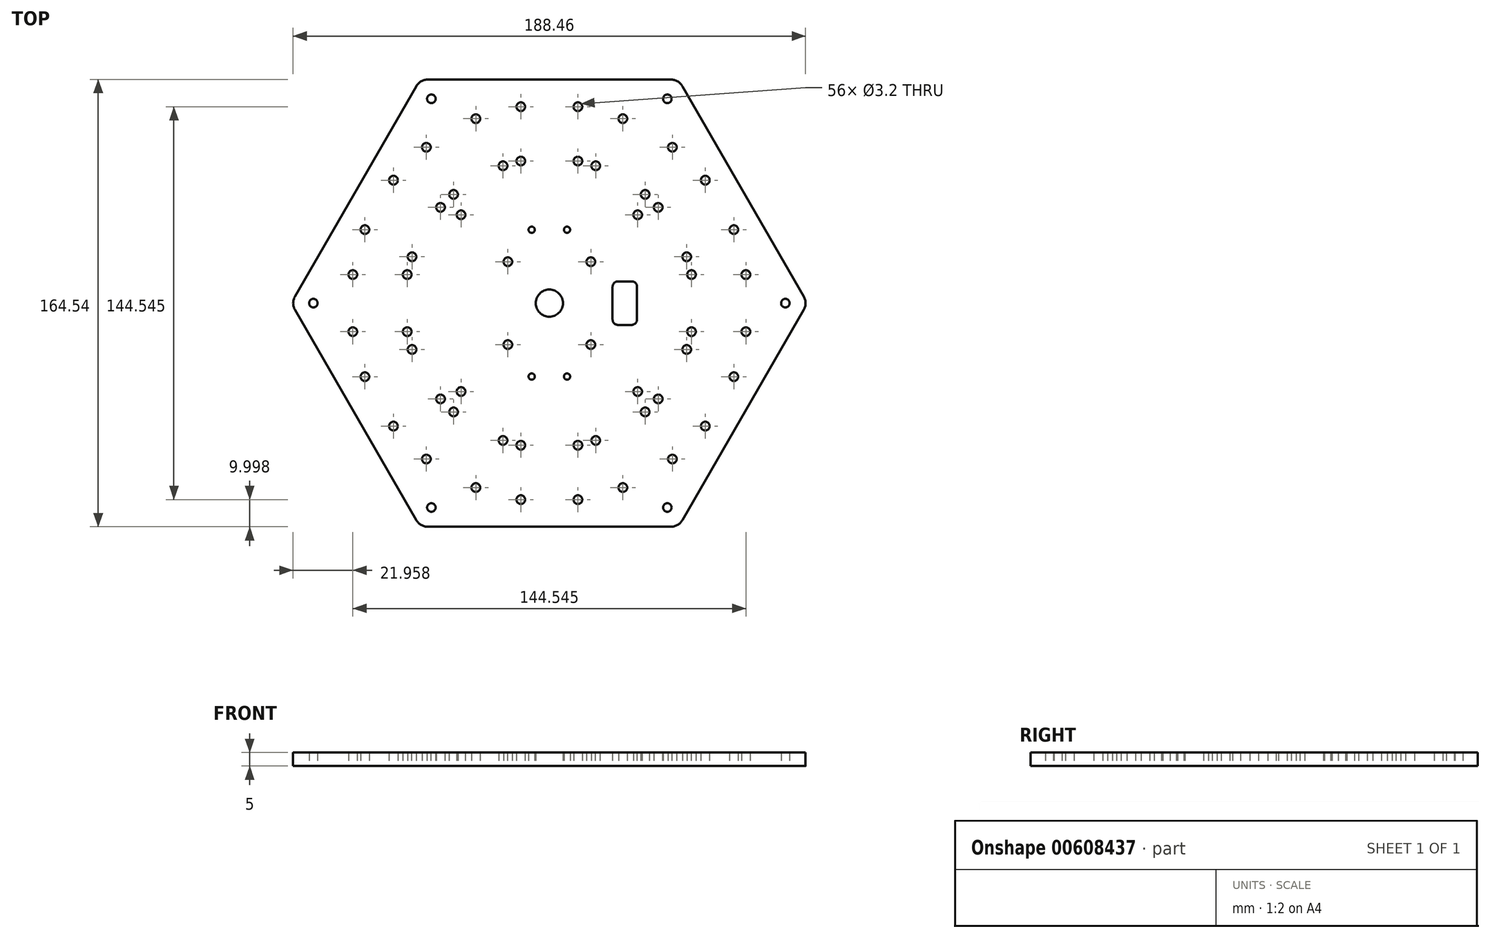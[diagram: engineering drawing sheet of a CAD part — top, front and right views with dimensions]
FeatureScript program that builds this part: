
annotation { "Feature Type Name" : "Feature", "Feature Type Description" : "" }
export const myFeature = defineFeature(function(context is Context, id is Id, definition is map)
    precondition{}
    {
        {
            var Q0;
            Q0=qCreatedBy(makeId("Top.planeOp"),FACE);
            var sketch = newSketch(context, id + "F0", { "sketchPlane" : qUnion([Q0])});
            skLineSegment(sketch, "E0.1", {"start": v(-48.94, -79.77) * mm, "end": v(-93.56, -2.5) * mm});
            skLineSegment(sketch, "E0.2", {"start": v(-93.56, 2.5) * mm, "end": v(-48.94, 79.77) * mm});
            skLineSegment(sketch, "E0.3", {"start": v(-44.61, 82.27) * mm, "end": v(44.61, 82.27) * mm});
            skLineSegment(sketch, "E0.4", {"start": v(48.94, 79.77) * mm, "end": v(93.56, 2.5) * mm});
            skLineSegment(sketch, "E0.5", {"start": v(93.56, -2.5) * mm, "end": v(48.94, -79.77) * mm});
            skPoint(sketch, "E0.cCircle.center.orphan", {"position": v(0, 0) * mm});
            skLineSegment(sketch, "E1", {"start": v(-44.61, -82.27) * mm, "end": v(44.61, -82.27) * mm});
            skPoint(sketch, "E2", {"position": v(-47.5, 82.27) * mm});
            skPoint(sketch, "E3", {"position": v(-43.4, 75.17) * mm});
            skCircle(sketch, "E4", {"center": v(-43.4, 75.17) * mm, "radius": 1.57 * mm});
            skCircle(sketch, "E5.1.0", {"center": v(-86.8, 0) * mm, "radius": 1.57 * mm});
            skCircle(sketch, "E5.2.0", {"center": v(-43.4, -75.17) * mm, "radius": 1.57 * mm});
            skCircle(sketch, "E5.3.0", {"center": v(43.4, -75.17) * mm, "radius": 1.57 * mm});
            skCircle(sketch, "E5.4.0", {"center": v(86.8, 0) * mm, "radius": 1.57 * mm});
            skCircle(sketch, "E5.5.0", {"center": v(43.4, 75.17) * mm, "radius": 1.57 * mm});
            skPoint(sketch, "E6", {"position": v(47.5, 82.27) * mm});
            skPoint(sketch, "E7", {"position": v(0, 82.27) * mm});
            skPoint(sketch, "E8", {"position": v(10.5, 82.27) * mm});
            skPoint(sketch, "E9", {"position": v(-10.5, 82.27) * mm});
            skPoint(sketch, "E10", {"position": v(-10.5, 72.27) * mm});
            skPoint(sketch, "E11", {"position": v(10.5, 72.27) * mm});
            skPoint(sketch, "E12", {"position": v(-10.5, 52.27) * mm});
            skPoint(sketch, "E13", {"position": v(10.5, 52.27) * mm});
            skCircle(sketch, "E14", {"center": v(-10.5, 72.27) * mm, "radius": 1.6 * mm});
            skCircle(sketch, "E15", {"center": v(10.5, 72.27) * mm, "radius": 1.6 * mm});
            skCircle(sketch, "E16", {"center": v(10.5, 52.27) * mm, "radius": 1.6 * mm});
            skCircle(sketch, "E17", {"center": v(-10.5, 52.27) * mm, "radius": 1.6 * mm});
            skPoint(sketch, "E18.1.0", {"position": v(-27.04, 67.84) * mm});
            skCircle(sketch, "E18.1.1", {"center": v(-27.04, 67.84) * mm, "radius": 1.6 * mm});
            skPoint(sketch, "E18.1.2", {"position": v(-45.23, 57.34) * mm});
            skCircle(sketch, "E18.1.3", {"center": v(-45.23, 57.34) * mm, "radius": 1.6 * mm});
            skPoint(sketch, "E18.1.4", {"position": v(-35.23, 40.02) * mm});
            skCircle(sketch, "E18.1.5", {"center": v(-35.23, 40.02) * mm, "radius": 1.6 * mm});
            skPoint(sketch, "E18.1.6", {"position": v(-17.04, 50.52) * mm});
            skCircle(sketch, "E18.1.7", {"center": v(-17.04, 50.52) * mm, "radius": 1.6 * mm});
            skPoint(sketch, "E18.2.0", {"position": v(-57.34, 45.23) * mm});
            skCircle(sketch, "E18.2.1", {"center": v(-57.34, 45.23) * mm, "radius": 1.6 * mm});
            skPoint(sketch, "E18.2.2", {"position": v(-67.84, 27.04) * mm});
            skCircle(sketch, "E18.2.3", {"center": v(-67.84, 27.04) * mm, "radius": 1.6 * mm});
            skPoint(sketch, "E18.2.4", {"position": v(-50.52, 17.04) * mm});
            skCircle(sketch, "E18.2.5", {"center": v(-50.52, 17.04) * mm, "radius": 1.6 * mm});
            skPoint(sketch, "E18.2.6", {"position": v(-40.02, 35.23) * mm});
            skCircle(sketch, "E18.2.7", {"center": v(-40.02, 35.23) * mm, "radius": 1.6 * mm});
            skPoint(sketch, "E18.3.0", {"position": v(-72.27, 10.5) * mm});
            skCircle(sketch, "E18.3.1", {"center": v(-72.27, 10.5) * mm, "radius": 1.6 * mm});
            skPoint(sketch, "E18.3.2", {"position": v(-72.27, -10.5) * mm});
            skCircle(sketch, "E18.3.3", {"center": v(-72.27, -10.5) * mm, "radius": 1.6 * mm});
            skPoint(sketch, "E18.3.4", {"position": v(-52.27, -10.5) * mm});
            skCircle(sketch, "E18.3.5", {"center": v(-52.27, -10.5) * mm, "radius": 1.6 * mm});
            skPoint(sketch, "E18.3.6", {"position": v(-52.27, 10.5) * mm});
            skCircle(sketch, "E18.3.7", {"center": v(-52.27, 10.5) * mm, "radius": 1.6 * mm});
            skPoint(sketch, "E18.4.0", {"position": v(-67.84, -27.04) * mm});
            skCircle(sketch, "E18.4.1", {"center": v(-67.84, -27.04) * mm, "radius": 1.6 * mm});
            skPoint(sketch, "E18.4.2", {"position": v(-57.34, -45.23) * mm});
            skCircle(sketch, "E18.4.3", {"center": v(-57.34, -45.23) * mm, "radius": 1.6 * mm});
            skPoint(sketch, "E18.4.4", {"position": v(-40.02, -35.23) * mm});
            skCircle(sketch, "E18.4.5", {"center": v(-40.02, -35.23) * mm, "radius": 1.6 * mm});
            skPoint(sketch, "E18.4.6", {"position": v(-50.52, -17.04) * mm});
            skCircle(sketch, "E18.4.7", {"center": v(-50.52, -17.04) * mm, "radius": 1.6 * mm});
            skPoint(sketch, "E18.5.0", {"position": v(-45.23, -57.34) * mm});
            skCircle(sketch, "E18.5.1", {"center": v(-45.23, -57.34) * mm, "radius": 1.6 * mm});
            skPoint(sketch, "E18.5.2", {"position": v(-27.04, -67.84) * mm});
            skCircle(sketch, "E18.5.3", {"center": v(-27.04, -67.84) * mm, "radius": 1.6 * mm});
            skPoint(sketch, "E18.5.4", {"position": v(-17.04, -50.52) * mm});
            skCircle(sketch, "E18.5.5", {"center": v(-17.04, -50.52) * mm, "radius": 1.6 * mm});
            skPoint(sketch, "E18.5.6", {"position": v(-35.23, -40.02) * mm});
            skCircle(sketch, "E18.5.7", {"center": v(-35.23, -40.02) * mm, "radius": 1.6 * mm});
            skPoint(sketch, "E19.left.end.orphan", {"position": v(32.5, 32.5) * mm});
            skPoint(sketch, "E19.bottom.start.orphan", {"position": v(32.5, -32.5) * mm});
            skPoint(sketch, "E19.right.end.orphan", {"position": v(-32.5, 32.5) * mm});
            skPoint(sketch, "E19.right.start.orphan", {"position": v(-32.5, -32.5) * mm});
            skCircle(sketch, "E20", {"center": v(-32.5, 32.5) * mm, "radius": 1.6 * mm});
            skCircle(sketch, "E21.1.1", {"center": v(-32.5, -32.5) * mm, "radius": 1.6 * mm});
            skCircle(sketch, "E21.2.1", {"center": v(32.5, -32.5) * mm, "radius": 1.6 * mm});
            skCircle(sketch, "E21.3.1", {"center": v(32.5, 32.5) * mm, "radius": 1.6 * mm});
            skPoint(sketch, "E22.visualSharp", {"position": v(47.5, -82.27) * mm});
            skArc(sketch, "E22.filletArc", {"start": v(44.61, -82.27) * mm, "mid": v(47.11, -81.6) * mm, "end": v(48.94, -79.77) * mm});
            skPoint(sketch, "E23.1.0", {"position": v(95, 0) * mm});
            skArc(sketch, "E23.1.1", {"start": v(93.56, -2.5) * mm, "mid": v(94.23, 0) * mm, "end": v(93.56, 2.5) * mm});
            skArc(sketch, "E23.2.1", {"start": v(48.94, 79.77) * mm, "mid": v(47.11, 81.6) * mm, "end": v(44.61, 82.27) * mm});
            skArc(sketch, "E23.3.1", {"start": v(-44.61, 82.27) * mm, "mid": v(-47.11, 81.6) * mm, "end": v(-48.94, 79.77) * mm});
            skPoint(sketch, "E23.4.0", {"position": v(-95, 0) * mm});
            skArc(sketch, "E23.4.1", {"start": v(-93.56, 2.5) * mm, "mid": v(-94.23, 0) * mm, "end": v(-93.56, -2.5) * mm});
            skPoint(sketch, "E23.5.0", {"position": v(-47.5, -82.27) * mm});
            skArc(sketch, "E23.5.1", {"start": v(-48.94, -79.77) * mm, "mid": v(-47.11, -81.6) * mm, "end": v(-44.61, -82.27) * mm});
            skPoint(sketch, "E24.0.6.0", {"position": v(-10.5, -72.27) * mm});
            skCircle(sketch, "E24.1.6.0", {"center": v(-10.5, -72.27) * mm, "radius": 1.6 * mm});
            skPoint(sketch, "E24.3.6.0", {"position": v(10.5, -72.27) * mm});
            skCircle(sketch, "E24.4.6.0", {"center": v(10.5, -72.27) * mm, "radius": 1.6 * mm});
            skPoint(sketch, "E24.6.6.0", {"position": v(10.5, -52.27) * mm});
            skCircle(sketch, "E24.7.6.0", {"center": v(10.5, -52.27) * mm, "radius": 1.6 * mm});
            skPoint(sketch, "E24.9.6.0", {"position": v(-10.5, -52.27) * mm});
            skCircle(sketch, "E24.10.6.0", {"center": v(-10.5, -52.27) * mm, "radius": 1.6 * mm});
            skPoint(sketch, "E24.0.7.0", {"position": v(27.04, -67.84) * mm});
            skCircle(sketch, "E24.1.7.0", {"center": v(27.04, -67.84) * mm, "radius": 1.6 * mm});
            skPoint(sketch, "E24.3.7.0", {"position": v(45.23, -57.34) * mm});
            skCircle(sketch, "E24.4.7.0", {"center": v(45.23, -57.34) * mm, "radius": 1.6 * mm});
            skPoint(sketch, "E24.6.7.0", {"position": v(35.23, -40.02) * mm});
            skCircle(sketch, "E24.7.7.0", {"center": v(35.23, -40.02) * mm, "radius": 1.6 * mm});
            skPoint(sketch, "E24.9.7.0", {"position": v(17.04, -50.52) * mm});
            skCircle(sketch, "E24.10.7.0", {"center": v(17.04, -50.52) * mm, "radius": 1.6 * mm});
            skPoint(sketch, "E24.0.8.0", {"position": v(57.34, -45.23) * mm});
            skCircle(sketch, "E24.1.8.0", {"center": v(57.34, -45.23) * mm, "radius": 1.6 * mm});
            skPoint(sketch, "E24.3.8.0", {"position": v(67.84, -27.04) * mm});
            skCircle(sketch, "E24.4.8.0", {"center": v(67.84, -27.04) * mm, "radius": 1.6 * mm});
            skPoint(sketch, "E24.6.8.0", {"position": v(50.52, -17.04) * mm});
            skCircle(sketch, "E24.7.8.0", {"center": v(50.52, -17.04) * mm, "radius": 1.6 * mm});
            skPoint(sketch, "E24.9.8.0", {"position": v(40.02, -35.23) * mm});
            skCircle(sketch, "E24.10.8.0", {"center": v(40.02, -35.23) * mm, "radius": 1.6 * mm});
            skPoint(sketch, "E24.0.9.0", {"position": v(72.27, -10.5) * mm});
            skCircle(sketch, "E24.1.9.0", {"center": v(72.27, -10.5) * mm, "radius": 1.6 * mm});
            skPoint(sketch, "E24.3.9.0", {"position": v(72.27, 10.5) * mm});
            skCircle(sketch, "E24.4.9.0", {"center": v(72.27, 10.5) * mm, "radius": 1.6 * mm});
            skPoint(sketch, "E24.6.9.0", {"position": v(52.27, 10.5) * mm});
            skCircle(sketch, "E24.7.9.0", {"center": v(52.27, 10.5) * mm, "radius": 1.6 * mm});
            skPoint(sketch, "E24.9.9.0", {"position": v(52.27, -10.5) * mm});
            skCircle(sketch, "E24.10.9.0", {"center": v(52.27, -10.5) * mm, "radius": 1.6 * mm});
            skPoint(sketch, "E24.0.10.0", {"position": v(67.84, 27.04) * mm});
            skCircle(sketch, "E24.1.10.0", {"center": v(67.84, 27.04) * mm, "radius": 1.6 * mm});
            skPoint(sketch, "E24.3.10.0", {"position": v(57.34, 45.23) * mm});
            skCircle(sketch, "E24.4.10.0", {"center": v(57.34, 45.23) * mm, "radius": 1.6 * mm});
            skPoint(sketch, "E24.6.10.0", {"position": v(40.02, 35.23) * mm});
            skCircle(sketch, "E24.7.10.0", {"center": v(40.02, 35.23) * mm, "radius": 1.6 * mm});
            skPoint(sketch, "E24.9.10.0", {"position": v(50.52, 17.04) * mm});
            skCircle(sketch, "E24.10.10.0", {"center": v(50.52, 17.04) * mm, "radius": 1.6 * mm});
            skPoint(sketch, "E24.0.11.0", {"position": v(45.23, 57.34) * mm});
            skCircle(sketch, "E24.1.11.0", {"center": v(45.23, 57.34) * mm, "radius": 1.6 * mm});
            skPoint(sketch, "E24.3.11.0", {"position": v(27.04, 67.84) * mm});
            skCircle(sketch, "E24.4.11.0", {"center": v(27.04, 67.84) * mm, "radius": 1.6 * mm});
            skPoint(sketch, "E24.6.11.0", {"position": v(17.04, 50.52) * mm});
            skCircle(sketch, "E24.7.11.0", {"center": v(17.04, 50.52) * mm, "radius": 1.6 * mm});
            skPoint(sketch, "E24.9.11.0", {"position": v(35.23, 40.02) * mm});
            skCircle(sketch, "E24.10.11.0", {"center": v(35.23, 40.02) * mm, "radius": 1.6 * mm});
            skLineSegment(sketch, "E25.bottom", {"start": v(15.25, -15.25) * mm, "end": v(-15.25, -15.25) * mm, "construction": true});
            skLineSegment(sketch, "E25.top", {"start": v(15.25, 15.25) * mm, "end": v(-15.25, 15.25) * mm, "construction": true});
            skLineSegment(sketch, "E25.left", {"start": v(15.25, -15.25) * mm, "end": v(15.25, 15.25) * mm, "construction": true});
            skLineSegment(sketch, "E25.right", {"start": v(-15.25, -15.25) * mm, "end": v(-15.25, 15.25) * mm, "construction": true});
            skLineSegment(sketch, "E26.bottom", {"start": v(25.25, 8) * mm, "end": v(30.25, 8) * mm});
            skLineSegment(sketch, "E26.top", {"start": v(25.25, -8) * mm, "end": v(30.25, -8) * mm});
            skLineSegment(sketch, "E26.left", {"start": v(23.25, 6) * mm, "end": v(23.25, -6) * mm});
            skLineSegment(sketch, "E26.right", {"start": v(32.25, 6) * mm, "end": v(32.25, -6) * mm});
            skCircle(sketch, "E27", {"center": v(-15.25, 15.25) * mm, "radius": 1.6 * mm});
            skCircle(sketch, "E28", {"center": v(15.25, 15.25) * mm, "radius": 1.6 * mm});
            skCircle(sketch, "E29", {"center": v(15.25, -15.25) * mm, "radius": 1.6 * mm});
            skCircle(sketch, "E30", {"center": v(-15.25, -15.25) * mm, "radius": 1.6 * mm});
            skPoint(sketch, "E31", {"position": v(23.25, 0) * mm});
            skPoint(sketch, "E32.visualSharp", {"position": v(23.25, 8) * mm});
            skArc(sketch, "E32.filletArc", {"start": v(25.25, 8) * mm, "mid": v(23.84, 7.41) * mm, "end": v(23.25, 6) * mm});
            skPoint(sketch, "E33.visualSharp", {"position": v(23.25, -8) * mm});
            skArc(sketch, "E33.filletArc", {"start": v(23.25, -6) * mm, "mid": v(23.84, -7.41) * mm, "end": v(25.25, -8) * mm});
            skPoint(sketch, "E34.visualSharp", {"position": v(32.25, 8) * mm});
            skArc(sketch, "E34.filletArc", {"start": v(32.25, 6) * mm, "mid": v(31.66, 7.41) * mm, "end": v(30.25, 8) * mm});
            skPoint(sketch, "E35.visualSharp", {"position": v(32.25, -8) * mm});
            skArc(sketch, "E35.filletArc", {"start": v(30.25, -8) * mm, "mid": v(31.66, -7.41) * mm, "end": v(32.25, -6) * mm});
            skLineSegment(sketch, "E36.bottom", {"start": v(6.5, 27) * mm, "end": v(-6.5, 27) * mm, "construction": true});
            skLineSegment(sketch, "E36.top", {"start": v(6.5, -27) * mm, "end": v(-6.5, -27) * mm, "construction": true});
            skLineSegment(sketch, "E36.left", {"start": v(6.5, 27) * mm, "end": v(6.5, -27) * mm, "construction": true});
            skLineSegment(sketch, "E36.right", {"start": v(-6.5, 27) * mm, "end": v(-6.5, -27) * mm, "construction": true});
            skCircle(sketch, "E37", {"center": v(-6.5, -27) * mm, "radius": 1.15 * mm});
            skCircle(sketch, "E38", {"center": v(6.5, -27) * mm, "radius": 1.15 * mm});
            skCircle(sketch, "E39", {"center": v(6.5, 27) * mm, "radius": 1.15 * mm});
            skCircle(sketch, "E40", {"center": v(-6.5, 27) * mm, "radius": 1.15 * mm});
            skCircle(sketch, "E41", {"center": v(0, 0) * mm, "radius": 5 * mm});
            skSolve(sketch);
        }
        {
            var Q0;
            Q0=makeQuery(id+"F0.imprint","IMPRINT",FACE,{"disambiguationData":[TD([[makeQuery(id+"F0.imprint","IMPRINT",EDGE,{"derivedFrom":sQuery(id+"F0.wireOp",EDGE,"E0.1")}),-1.0]])]});
            extrude(context, id + "F1", {"entities" : qUnion([Q0]), "flatOperationType" : FlatOperationType.REMOVE, "depth" : 5 * mm, "offsetDistance" : 25 * mm, "domain" : OperationDomain.MODEL});
        }
    });
